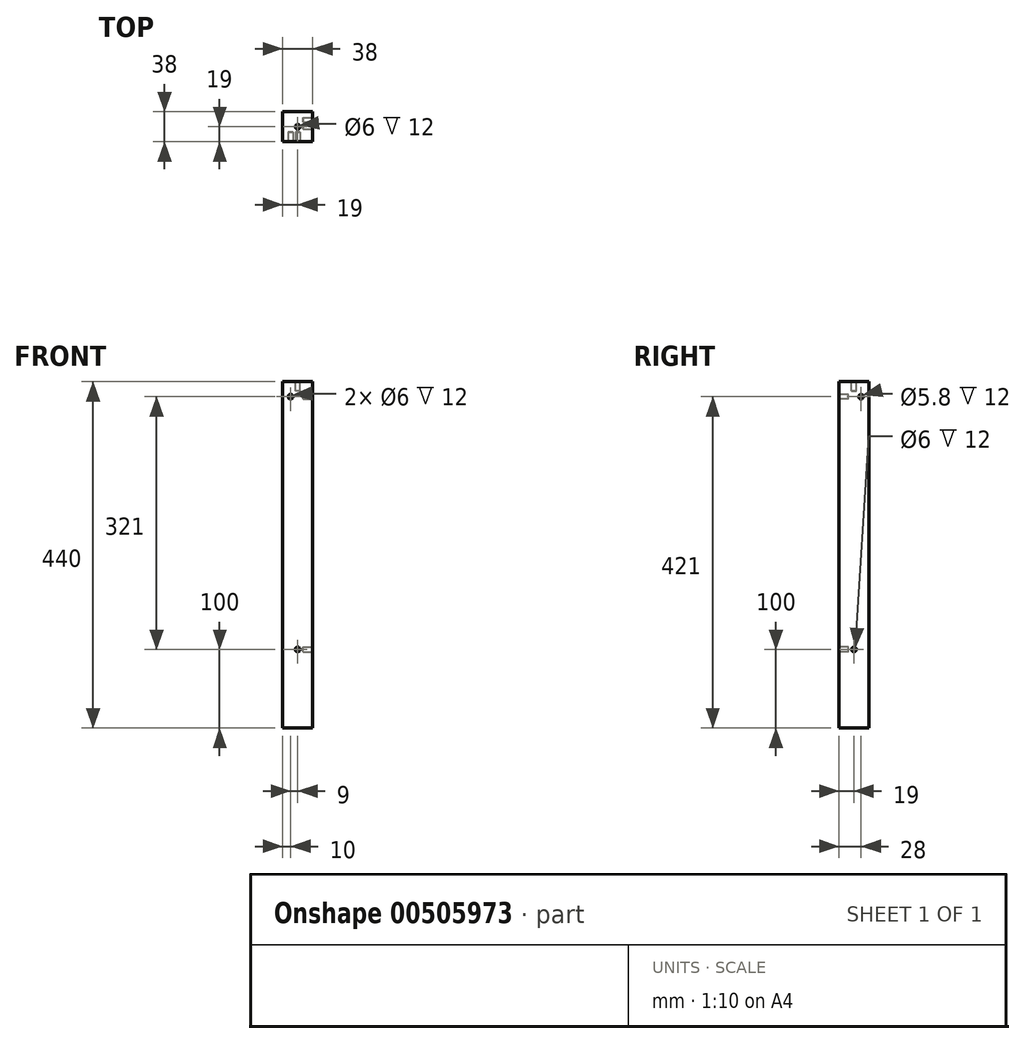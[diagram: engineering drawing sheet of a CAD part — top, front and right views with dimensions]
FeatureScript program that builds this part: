
annotation { "Feature Type Name" : "Feature", "Feature Type Description" : "" }
export const myFeature = defineFeature(function(context is Context, id is Id, definition is map)
    precondition{}
    {
        {
            var Q0;
            Q0=qCreatedBy(makeId("Top.planeOp"),FACE);
            var sketch = newSketch(context, id + "F0", { "sketchPlane" : qUnion([Q0])});
            skLineSegment(sketch, "E0.bottom", {"start": v(0, 0) * mm, "end": v(38, 0) * mm});
            skLineSegment(sketch, "E0.top", {"start": v(0, 38) * mm, "end": v(38, 38) * mm});
            skLineSegment(sketch, "E0.left", {"start": v(0, 0) * mm, "end": v(0, 38) * mm});
            skLineSegment(sketch, "E0.right", {"start": v(38, 0) * mm, "end": v(38, 38) * mm});
            skSolve(sketch);
        }
        {
            var Q0;
            Q0=qSketchRegion(id+"F0",true);
            extrude(context, id + "F1", {"entities" : qUnion([Q0]), "depth" : 440 * mm, "offsetDistance" : 25 * mm});
        }
        {
            var Q0;
            Q0=makeQuery(id+"F1.opExtrude","SWEPT_FACE",FACE,{"disambiguationData":[OSD([sQuery(id+"F0.wireOp",EDGE,"E0.bottom")])]});
            var sketch = newSketch(context, id + "F2", { "sketchPlane" : qUnion([Q0])});
            skCircle(sketch, "E1", {"center": v(10, 421) * mm, "radius": 3 * mm});
            skSolve(sketch);
        }
        {
            var Q0;
            Q0 = qSketchRegion(id + "F2", true);
            extrude(context, id + "F3", {"entities" : qUnion([Q0]), "operationType" : NewBodyOperationType.REMOVE, "oppositeDirection" : true, "depth" : 12 * mm, "offsetDistance" : 25 * mm});
        }
        {
            var Q0;
            Q0=makeQuery(id+"F1.opExtrude","SWEPT_FACE",FACE,{"disambiguationData":[OSD([sQuery(id+"F0.wireOp",EDGE,"E0.right")])]});
            var sketch = newSketch(context, id + "F4", { "sketchPlane" : qUnion([Q0])});
            skCircle(sketch, "E2", {"center": v(28, 421) * mm, "radius": 2.9 * mm});
            skSolve(sketch);
        }
        {
            var Q0;
            Q0 = qSketchRegion(id + "F4", true);
            extrude(context, id + "F5", {"entities" : qUnion([Q0]), "operationType" : NewBodyOperationType.REMOVE, "oppositeDirection" : true, "depth" : 12 * mm, "offsetDistance" : 25 * mm});
        }
        {
            var Q0;
            Q0=makeQuery(id+"F1.opExtrude","CAP_FACE",FACE,{"disambiguationData":[OSD([sQuery(id+"F0.wireOp",EDGE,"E0.bottom"),sQuery(id+"F0.wireOp",EDGE,"E0.top"),sQuery(id+"F0.wireOp",EDGE,"E0.left"),sQuery(id+"F0.wireOp",EDGE,"E0.right")])],"isStart":false});
            var sketch = newSketch(context, id + "F6", { "sketchPlane" : qUnion([Q0])});
            skCircle(sketch, "E3", {"center": v(19, 19) * mm, "radius": 3 * mm});
            skSolve(sketch);
        }
        {
            var Q0;
            Q0=makeQuery(id+"F6.imprint","IMPRINT",FACE,{"disambiguationData":[TD([[makeQuery(id+"F6.imprint","IMPRINT",EDGE,{"derivedFrom":sQuery(id+"F6.wireOp",EDGE,"E3")}),1.0]])]});
            extrude(context, id + "F7", {"entities" : qUnion([Q0]), "operationType" : NewBodyOperationType.REMOVE, "oppositeDirection" : true, "depth" : 12 * mm, "offsetDistance" : 25 * mm});
        }
        {
            var Q0;
            Q0=makeQuery(id+"F1.opExtrude","SWEPT_FACE",FACE,{"disambiguationData":[OSD([sQuery(id+"F0.wireOp",EDGE,"E0.bottom")])]});
            var sketch = newSketch(context, id + "F8", { "sketchPlane" : qUnion([Q0])});
            skCircle(sketch, "E4", {"center": v(19, 100) * mm, "radius": 3 * mm});
            skSolve(sketch);
        }
        {
            var Q0;
            Q0 = qSketchRegion(id + "F8", true);
            extrude(context, id + "F9", {"entities" : qUnion([Q0]), "operationType" : NewBodyOperationType.REMOVE, "oppositeDirection" : true, "depth" : 12 * mm, "offsetDistance" : 25 * mm});
        }
        {
            var Q0;
            Q0=makeQuery(id+"F1.opExtrude","SWEPT_FACE",FACE,{"disambiguationData":[OSD([sQuery(id+"F0.wireOp",EDGE,"E0.right")])]});
            var sketch = newSketch(context, id + "F10", { "sketchPlane" : qUnion([Q0])});
            skCircle(sketch, "E5", {"center": v(19, 100) * mm, "radius": 3 * mm});
            skSolve(sketch);
        }
        {
            var Q0;
            Q0 = qSketchRegion(id + "F10", true);
            extrude(context, id + "F11", {"entities" : qUnion([Q0]), "operationType" : NewBodyOperationType.REMOVE, "oppositeDirection" : true, "depth" : 12 * mm, "offsetDistance" : 25 * mm});
        }
        {
            var Q0;
            Q0 = qSketchRegion(id + "F6", true);
            extrude(context, id + "F12", {"entities" : qUnion([Q0]), "operationType" : NewBodyOperationType.REMOVE, "oppositeDirection" : true, "depth" : 12 * mm, "offsetDistance" : 25 * mm});
        }
    });
